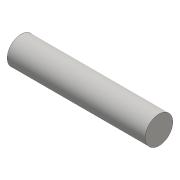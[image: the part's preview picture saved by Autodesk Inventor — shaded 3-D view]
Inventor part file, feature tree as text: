
AUTODESK INVENTOR PART (.ipt)
format: ipt  version: 2016 (Build 200138000, 138)  size: 68,096 bytes
history: native  units: mm
features: extrude x1, sketch x1
ambient origin geometry x8: Origin, YZ Plane, XZ Plane, XY Plane, X Axis, Y Axis, Z Axis, Center Point
bodies: Solid1 (feature_tree)
feature tree (2):
  extrude  "Extrusion1"  Depth=31.75mm TaperAngle=0.0deg
  sketch  "Sketch1"  dims[d0=6.35mm d1=31.75mm d2=0.0mm]
